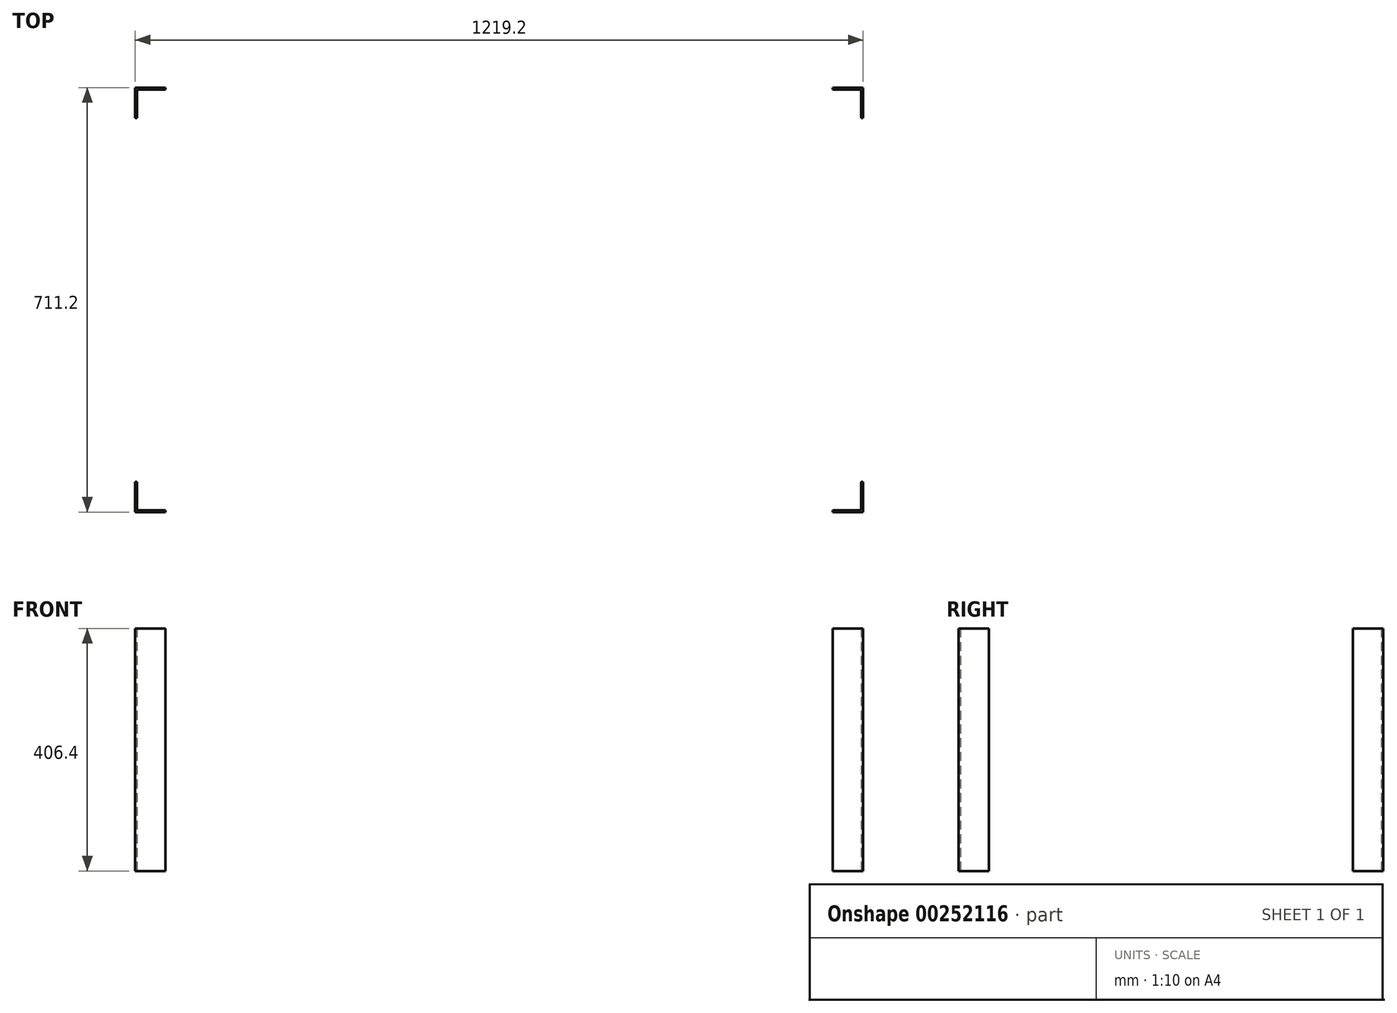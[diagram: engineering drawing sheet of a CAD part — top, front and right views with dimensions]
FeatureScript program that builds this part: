
annotation { "Feature Type Name" : "Feature", "Feature Type Description" : "" }
export const myFeature = defineFeature(function(context is Context, id is Id, definition is map)
    precondition{}
    {
        {
            var Q0;
            Q0=qCreatedBy(makeId("Top.planeOp"),FACE);
            var sketch = newSketch(context, id + "F0", { "sketchPlane" : qUnion([Q0])});
            skLineSegment(sketch, "E0.bottom", {"start": v(609.6, 355.6) * mm, "end": v(558.8, 355.6) * mm});
            skLineSegment(sketch, "E0.top", {"start": v(609.6, -355.6) * mm, "end": v(558.8, -355.6) * mm});
            skLineSegment(sketch, "E0.left", {"start": v(609.6, 355.6) * mm, "end": v(609.6, 304.8) * mm});
            skLineSegment(sketch, "E0.right", {"start": v(-609.6, 355.6) * mm, "end": v(-609.6, 304.8) * mm});
            skPoint(sketch, "E0.middle", {"position": v(0, 0) * mm});
            skLineSegment(sketch, "E1.bottom", {"start": v(606.43, 352.43) * mm, "end": v(558.8, 352.43) * mm});
            skLineSegment(sketch, "E1.top", {"start": v(606.43, -352.43) * mm, "end": v(558.8, -352.43) * mm});
            skLineSegment(sketch, "E1.left", {"start": v(606.43, 352.43) * mm, "end": v(606.43, 304.8) * mm});
            skLineSegment(sketch, "E1.right", {"start": v(-606.43, 352.43) * mm, "end": v(-606.43, 304.8) * mm});
            skLineSegment(sketch, "E2.bottom", {"start": v(-609.6, 355.6) * mm, "end": v(-558.8, 355.6) * mm});
            skLineSegment(sketch, "E2.top", {"start": v(-609.6, 304.8) * mm, "end": v(-606.43, 304.8) * mm});
            skLineSegment(sketch, "E2.right", {"start": v(-558.8, 355.6) * mm, "end": v(-558.8, 352.43) * mm});
            skLineSegment(sketch, "E3.top", {"start": v(609.6, 304.8) * mm, "end": v(606.43, 304.8) * mm});
            skLineSegment(sketch, "E3.right", {"start": v(558.8, 355.6) * mm, "end": v(558.8, 352.43) * mm});
            skLineSegment(sketch, "E4.top", {"start": v(609.6, -304.8) * mm, "end": v(606.43, -304.8) * mm});
            skLineSegment(sketch, "E4.left", {"start": v(609.6, -355.6) * mm, "end": v(609.6, -304.8) * mm});
            skLineSegment(sketch, "E4.right", {"start": v(558.8, -355.6) * mm, "end": v(558.8, -352.43) * mm});
            skLineSegment(sketch, "E5.bottom", {"start": v(-609.6, -355.6) * mm, "end": v(-558.8, -355.6) * mm});
            skLineSegment(sketch, "E5.top", {"start": v(-609.6, -304.8) * mm, "end": v(-606.43, -304.8) * mm});
            skLineSegment(sketch, "E5.left", {"start": v(-609.6, -355.6) * mm, "end": v(-609.6, -304.8) * mm});
            skLineSegment(sketch, "E5.right", {"start": v(-558.8, -355.6) * mm, "end": v(-558.8, -352.43) * mm});
            skLineSegment(sketch, "E6.trimOffspring", {"start": v(-609.6, -304.8) * mm, "end": v(-609.6, -355.6) * mm});
            skLineSegment(sketch, "E7.trimOffspring", {"start": v(-606.43, -304.8) * mm, "end": v(-606.43, -352.43) * mm});
            skLineSegment(sketch, "E8.trimOffspring", {"start": v(-558.8, -352.43) * mm, "end": v(-606.43, -352.43) * mm});
            skLineSegment(sketch, "E9.trimOffspring", {"start": v(-558.8, -355.6) * mm, "end": v(-609.6, -355.6) * mm});
            skLineSegment(sketch, "E10.trimOffspring", {"start": v(-558.8, 355.6) * mm, "end": v(-609.6, 355.6) * mm});
            skLineSegment(sketch, "E11.trimOffspring", {"start": v(-558.8, 352.43) * mm, "end": v(-606.43, 352.43) * mm});
            skLineSegment(sketch, "E12.trimOffspring", {"start": v(606.43, -304.8) * mm, "end": v(606.43, -352.43) * mm});
            skLineSegment(sketch, "E13.trimOffspring", {"start": v(609.6, -304.8) * mm, "end": v(609.6, -355.6) * mm});
            skSolve(sketch);
        }
        {
            var Q0;
            Q0=makeQuery(id+"F0.imprint","IMPRINT",FACE,{"disambiguationData":[TD([[makeQuery(id+"F0.imprint","IMPRINT",EDGE,{"derivedFrom":sQuery(id+"F0.wireOp",EDGE,"E1.right")}),-1.0]])]});
            var Q1;
            Q1=makeQuery(id+"F0.imprint","IMPRINT",FACE,{"disambiguationData":[TD([[makeQuery(id+"F0.imprint","IMPRINT",EDGE,{"derivedFrom":sQuery(id+"F0.wireOp",EDGE,"E5.top")}),-1.0]])]});
            var Q2;
            Q2=makeQuery(id+"F0.imprint","IMPRINT",FACE,{"disambiguationData":[TD([[makeQuery(id+"F0.imprint","IMPRINT",EDGE,{"derivedFrom":sQuery(id+"F0.wireOp",EDGE,"E1.top")}),1.0]])]});
            var Q3;
            Q3=makeQuery(id+"F0.imprint","IMPRINT",FACE,{"disambiguationData":[TD([[makeQuery(id+"F0.imprint","IMPRINT",EDGE,{"derivedFrom":sQuery(id+"F0.wireOp",EDGE,"E1.bottom")}),-1.0]])]});
            extrude(context, id + "F1", {"entities" : qUnion([Q0, Q1, Q2, Q3]), "depth" : 406.4 * mm});
        }
    });
